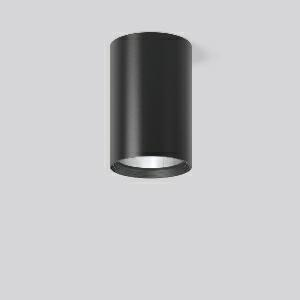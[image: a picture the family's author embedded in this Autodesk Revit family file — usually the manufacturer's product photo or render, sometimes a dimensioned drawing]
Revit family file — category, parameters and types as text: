
# Revit family: heledon_maxi_a_931216_003_1_92eb
name_source: partatom
category: Lighting Fixtures
units: mm (PartAtom-declared; Revit-internal decimal feet)

## family parameters
Cut with Voids When Loaded = No
Host = Face
Light Source = No
Part Type = Normal
Room Calculation Point = No
Round Connector Dimension = Use Diameter
Shared = No

## types (1)
- HELEDON maxi A (1 x LED Modul 940, 3400 lm, 4000)
    Apparent Load = 25 VA
    Approval mark = CE
    CIE Flux Codes = 100 100 100 100 100
    Color Rendering = 92
    Color Temperature = 4000
    Default Elevation = 1800 mm
    Description = Series: HELEDON maxi
Cylindrical surface-mounted downlight. Housing: die-cast aluminium, powder-coated. Internal ceiling frame polycarbonate with bayonet mounting. Black plastic ring and recessed LED to prevent glare from the side. Optical assembly with reflector made of MIRO-Silver with 98% total light reflection for outstanding efficiency - can be changed without tools. Best colour rendering index Ra>90. Suitable for Ceiling mounting. Easy installation with a separate ceiling frame with bayonet mounting and plug connection. Driver integrated. Connected via plug-in connector. High quality converter without flickering and stroboscopic effect. The following accessories can be mounted without use of tools: interchangeable lenses, decorative glasses, honeycomb louvre, clear and frosted diffusers, white interchangeable plastic ring. 
Colour: deep black, matt (RAL 9005)
Diameter: 123 mm
Height: 183 mm
Lamp: LED
Socket: without socket
Colour temperature: 4000K
Colour rendering index (CRI): 92
System power: 25 W
Rated luminous flux: 3400 lm
Luminous efficiency: 136 lm/W
Control gear: Regulated power supply
Protection class: I
Type of protection: IP 20
    Height = 183 mm
    Lamp = 1 x LED Modul 940
    Lamp Light Flux = 3400 lm
    Lamp count = 1
    Length = 123 mm
    Lifetime = 50000 h
    Luminous efficacy = 136 lm/W
    Manufacturer = RZB
    ModVariant = No
    Model = 931216.003.1
    Mounting Place = Ceiling
    Mounting Type = Surface mounted
    Number of Poles = 1
    OnlyDefault = Yes
    Power Factor = 1
    Product Name = HELEDON maxi A
    Product group = Surface mounted downlights
    ProductGroupID = 302
    Protection Class = Protection class I
    Protection Degree = IP 20
    RLX_Detail_Level = 1
    RLX_Emergency_Light_Flux = 0 lm
    RLX_Emergency_Type = 0
    RLX_Emergency_Type_DB = No
    RlxData = <blob elided: 98717 chars, md5=d83e7a74>
    Socket = socket
    Standby Power = 0 W
    System Light Flux = 3400 lm
    System Power = 25 W
    Type Comments = Product without accessories
    Type Image = 931192.003.jpg
    URL = http://relux.com
    VarID = ---
    Voltage = 230 V
    Voltage Range = 220-240 V
    Weight = 0.00 kg
    Width = 0 mm  [stored 0 ft]

note: [stored X ft] marks values corroborated as IEEE doubles in the binary element streams (Revit-internal decimal feet)

## geometry (parser evidence)
native form markers: Blend x4, Sweep x11
no freeform markers — native parametric forms only
